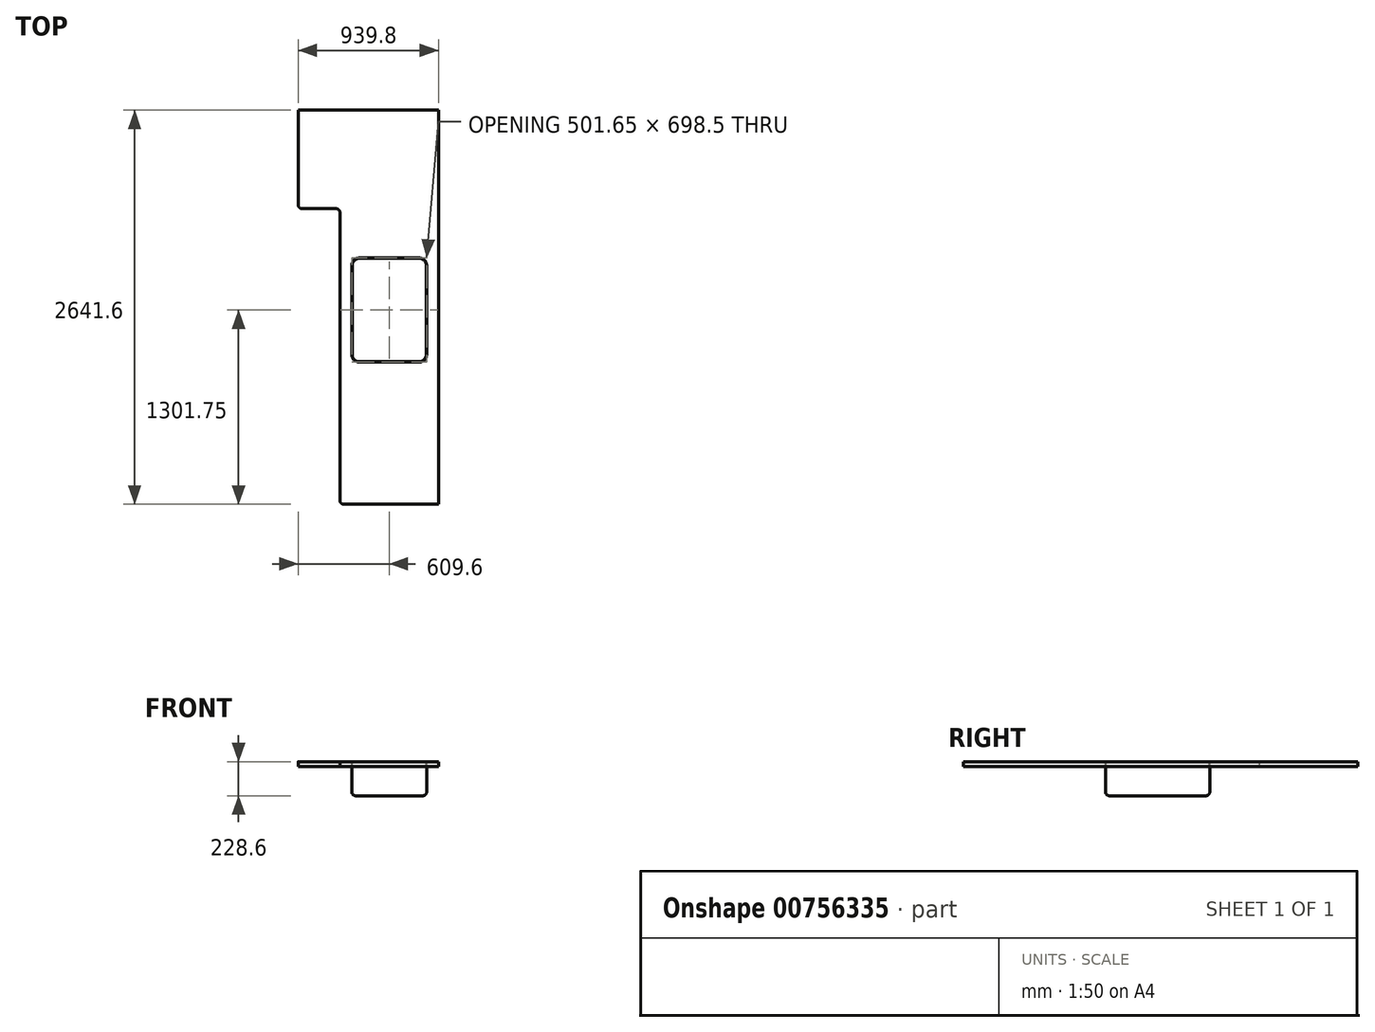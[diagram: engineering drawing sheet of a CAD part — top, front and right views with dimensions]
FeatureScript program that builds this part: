
annotation { "Feature Type Name" : "Feature", "Feature Type Description" : "" }
export const myFeature = defineFeature(function(context is Context, id is Id, definition is map)
    precondition{}
    {
        {
            var Q0;
            Q0=qCreatedBy(makeId("Top.planeOp"),FACE);
            var sketch = newSketch(context, id + "F0", { "sketchPlane" : qUnion([Q0])});
            skLineSegment(sketch, "E0.bottom", {"start": v(25.4, 0) * mm, "end": v(660.4, 0) * mm});
            skLineSegment(sketch, "E0.left", {"start": v(0, 25.4) * mm, "end": v(0, 1955.8) * mm});
            skLineSegment(sketch, "E0.right", {"start": v(660.4, 0) * mm, "end": v(660.4, 2641.6) * mm});
            skLineSegment(sketch, "E1.top", {"start": v(-25.4, 1981.2) * mm, "end": v(-254, 1981.2) * mm});
            skLineSegment(sketch, "E2", {"start": v(660.4, 2641.6) * mm, "end": v(-279.4, 2641.6) * mm});
            skLineSegment(sketch, "E3", {"start": v(-279.4, 2641.6) * mm, "end": v(-279.4, 2006.6) * mm});
            skLineSegment(sketch, "E4.bottom", {"start": v(130.17, 1651) * mm, "end": v(530.22, 1651) * mm});
            skLineSegment(sketch, "E4.top", {"start": v(130.17, 952.5) * mm, "end": v(530.22, 952.5) * mm});
            skLineSegment(sketch, "E4.left", {"start": v(79.37, 1600.2) * mm, "end": v(79.37, 1003.3) * mm});
            skLineSegment(sketch, "E4.right", {"start": v(581.02, 1600.2) * mm, "end": v(581.02, 1003.3) * mm});
            skPoint(sketch, "E5.visualSharp", {"position": v(79.37, 1651) * mm});
            skArc(sketch, "E5.filletArc", {"start": v(130.17, 1651) * mm, "mid": v(94.25, 1636.12) * mm, "end": v(79.37, 1600.2) * mm});
            skPoint(sketch, "E6.visualSharp", {"position": v(581.02, 1651) * mm});
            skArc(sketch, "E6.filletArc", {"start": v(581.02, 1600.2) * mm, "mid": v(566.15, 1636.12) * mm, "end": v(530.22, 1651) * mm});
            skPoint(sketch, "E7.visualSharp", {"position": v(581.02, 952.5) * mm});
            skArc(sketch, "E7.filletArc", {"start": v(530.22, 952.5) * mm, "mid": v(566.15, 967.38) * mm, "end": v(581.02, 1003.3) * mm});
            skPoint(sketch, "E8.visualSharp", {"position": v(79.37, 952.5) * mm});
            skArc(sketch, "E8.filletArc", {"start": v(79.37, 1003.3) * mm, "mid": v(94.25, 967.38) * mm, "end": v(130.17, 952.5) * mm});
            skPoint(sketch, "E9.visualSharp", {"position": v(0, 1981.2) * mm});
            skArc(sketch, "E9.filletArc", {"start": v(0, 1955.8) * mm, "mid": v(-7.44, 1973.76) * mm, "end": v(-25.4, 1981.2) * mm});
            skPoint(sketch, "E10.visualSharp", {"position": v(0, 0) * mm});
            skArc(sketch, "E10.filletArc", {"start": v(0, 25.4) * mm, "mid": v(7.44, 7.44) * mm, "end": v(25.4, 0) * mm});
            skPoint(sketch, "E11.visualSharp", {"position": v(-279.4, 1981.2) * mm});
            skArc(sketch, "E11.filletArc", {"start": v(-279.4, 2006.6) * mm, "mid": v(-271.96, 1988.64) * mm, "end": v(-254, 1981.2) * mm});
            skSolve(sketch);
        }
        {
            var Q0;
            Q0=makeQuery(id+"F0.imprint","IMPRINT",FACE,{"disambiguationData":[TD([[makeQuery(id+"F0.imprint","IMPRINT",EDGE,{"derivedFrom":sQuery(id+"F0.wireOp",EDGE,"E0.bottom")}),1.0]])]});
            extrude(context, id + "F1", {"entities" : qUnion([Q0]), "depth" : 31.75 * mm, "offsetDistance" : 25.4 * mm});
        }
        {
            var Q0;
            Q0=makeQuery(id+"F1.opExtrude","CAP_FACE",FACE,{"disambiguationData":[OSD([sQuery(id+"F0.wireOp",EDGE,"E0.bottom"),sQuery(id+"F0.wireOp",EDGE,"E0.left"),sQuery(id+"F0.wireOp",EDGE,"E0.right"),sQuery(id+"F0.wireOp",EDGE,"E1.top"),sQuery(id+"F0.wireOp",EDGE,"E2"),sQuery(id+"F0.wireOp",EDGE,"E3"),sQuery(id+"F0.wireOp",EDGE,"E4.bottom"),sQuery(id+"F0.wireOp",EDGE,"E4.top"),sQuery(id+"F0.wireOp",EDGE,"E4.left"),sQuery(id+"F0.wireOp",EDGE,"E4.right"),sQuery(id+"F0.wireOp",EDGE,"E5.filletArc"),sQuery(id+"F0.wireOp",EDGE,"E6.filletArc"),sQuery(id+"F0.wireOp",EDGE,"E7.filletArc"),sQuery(id+"F0.wireOp",EDGE,"E8.filletArc"),sQuery(id+"F0.wireOp",EDGE,"E9.filletArc"),sQuery(id+"F0.wireOp",EDGE,"E10.filletArc")])],"isStart":false});
            var sketch = newSketch(context, id + "F2", { "sketchPlane" : qUnion([Q0])});
            skArc(sketch, "E12.0.0", {"start": v(79.37, 1003.3) * mm, "mid": v(94.25, 967.38) * mm, "end": v(130.17, 952.5) * mm});
            skLineSegment(sketch, "E12.0.1", {"start": v(130.17, 952.5) * mm, "end": v(530.22, 952.5) * mm});
            skArc(sketch, "E12.0.2", {"start": v(530.22, 952.5) * mm, "mid": v(566.15, 967.38) * mm, "end": v(581.02, 1003.3) * mm});
            skLineSegment(sketch, "E12.0.3", {"start": v(581.02, 1003.3) * mm, "end": v(581.02, 1600.2) * mm});
            skArc(sketch, "E12.0.4", {"start": v(581.02, 1600.2) * mm, "mid": v(566.15, 1636.12) * mm, "end": v(530.22, 1651) * mm});
            skLineSegment(sketch, "E12.0.5", {"start": v(530.22, 1651) * mm, "end": v(130.17, 1651) * mm});
            skArc(sketch, "E12.0.6", {"start": v(130.17, 1651) * mm, "mid": v(94.25, 1636.12) * mm, "end": v(79.37, 1600.2) * mm});
            skLineSegment(sketch, "E12.0.7", {"start": v(79.37, 1600.2) * mm, "end": v(79.37, 1003.3) * mm});
            skSolve(sketch);
        }
        {
            var Q0;
            Q0=makeQuery(id+"F2.imprint","IMPRINT",FACE,{"disambiguationData":[TD([[makeQuery(id+"F2.imprint","IMPRINT",EDGE,{"derivedFrom":sQuery(id+"F2.wireOp",EDGE,"E12.0.0")}),1.0]])]});
            extrude(context, id + "F3", {"entities" : qUnion([Q0]), "oppositeDirection" : true, "depth" : 228.6 * mm, "offsetDistance" : 25.4 * mm});
        }
        {
            var Q0;
            Q0=makeQuery(id+"F3.opExtrude","CAP_FACE",FACE,{"disambiguationData":[OSD([sQuery(id+"F2.wireOp",EDGE,"E12.0.0"),sQuery(id+"F2.wireOp",EDGE,"E12.0.1"),sQuery(id+"F2.wireOp",EDGE,"E12.0.2"),sQuery(id+"F2.wireOp",EDGE,"E12.0.3"),sQuery(id+"F2.wireOp",EDGE,"E12.0.4"),sQuery(id+"F2.wireOp",EDGE,"E12.0.5"),sQuery(id+"F2.wireOp",EDGE,"E12.0.6"),sQuery(id+"F2.wireOp",EDGE,"E12.0.7")])],"isStart":true});
            shell(context, id + "F4", {"entities" : qUnion([Q0]), "thickness" : 2.54 * mm});
        }
        {
            var Q0;
            {var subQ0=sQuery(id+"F2.wireOp",EDGE,"E12.0.5");Q0=makeQuery(id+"F4.opShell","OFFSET_EDGE",EDGE,{"disambiguationData":[OSD([subQ0]),TDD([makeQuery(id+"F3.opExtrude","CAP_EDGE",EDGE,{"disambiguationData":[OSD([subQ0])],"isStart":false})])]});}
            fillet(context, id + "F5", {"entities" : qUnion([Q0]), "radius" : 25.4 * mm, "tangentPropagation" : true, "allowEdgeOverflow" : false});
        }
        {
            var Q0;
            Q0=makeQuery(id+"F3.opExtrude","CAP_EDGE",EDGE,{"disambiguationData":[OSD([sQuery(id+"F2.wireOp",EDGE,"E12.0.3")])],"isStart":false});
            fillet(context, id + "F6", {"entities" : qUnion([Q0]), "radius" : 25.4 * mm, "tangentPropagation" : true, "allowEdgeOverflow" : false});
        }
    });
